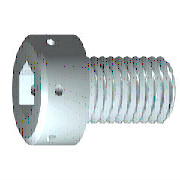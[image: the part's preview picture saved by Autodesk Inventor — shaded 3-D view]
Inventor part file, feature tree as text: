
AUTODESK INVENTOR PART (.ipt)
format: ipt  version: 2018.1 (Build 221171000, 171)  size: 247,296 bytes
history: native  units: mm (DEFAULTED — no unit token found)
features: sketch x4, extrude x3, pattern_circular x1, other x1, plane x1
ambient origin geometry x7: Origin, YZ Plane, XY Plane, X Axis, Y Axis, Z Axis, Center Point
bodies: Solid1 (feature_tree), Body (feature_tree)
feature tree (10):
  extrude  "Slot"  Depth=3.0mm
  extrude  "Overcut"  Depth=6.0mm
  extrude  "Hole"  Depth=10.0mm
  pattern_circular  "Holes"  [2 undecoded]
  other  "Work Axis1"
  plane  "Work Plane1"
  sketch  "Sketch1"  dims[d3=6.0mm d4=3.0mm]
  sketch  "Sketch2"  dims[d5=60.0deg d6=6.0mm]
  sketch  "Sketch4"  dims[d10=90.0deg d11=10.0mm d12=0.0mm d13=1.35mm d14=2.3mm d15=10.0mm d16=0.0mm d17=0.6mm d18=45.0deg d19=18.7731mm d20=0.0mm d21=0.61345mm d22=0.61345mm d23=0.57735mm d24=3.0mm d25=0.0mm d26=30.0mm d28=360.0deg d30=0.0mm d31=20.0mm d32=0.6mm d33=45.0deg d35=0.0mm d36=0.0mm]
  sketch  "Sketch3"  dims[d8=5.773503mm d9=10.0mm]
note: 2 required parameter values undecoded (feature->parameter linkage not recoverable at this tier; creation-order binding heuristic only, values carry confidence <= 0.55)
